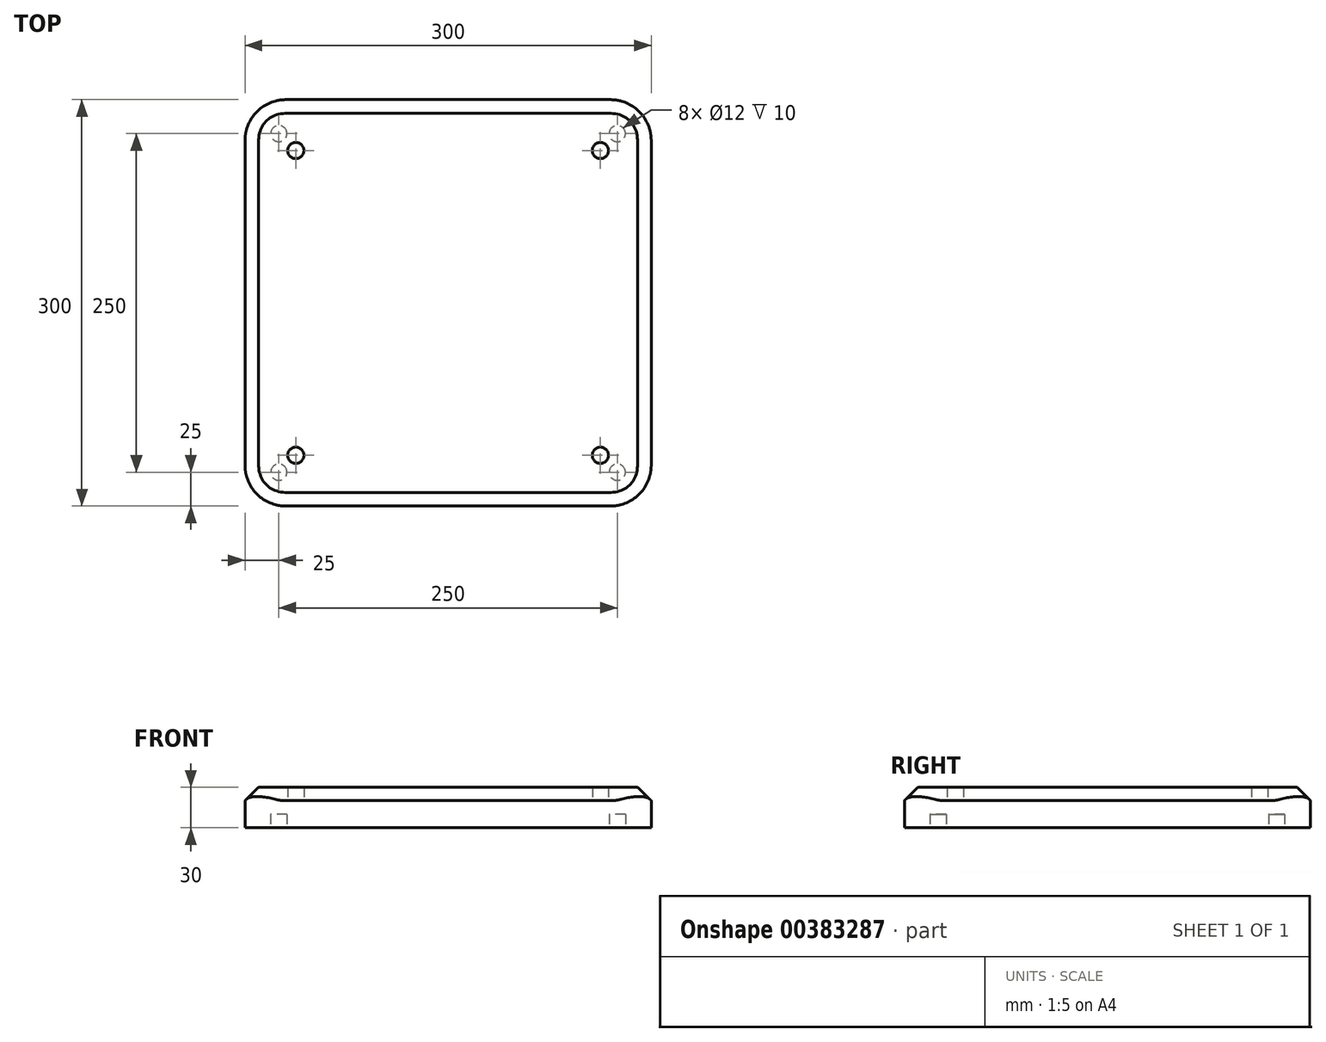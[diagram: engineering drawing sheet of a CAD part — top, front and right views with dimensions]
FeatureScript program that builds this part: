
annotation { "Feature Type Name" : "Feature", "Feature Type Description" : "" }
export const myFeature = defineFeature(function(context is Context, id is Id, definition is map)
    precondition{}
    {
        {
            var Q0;
            Q0=qCreatedBy(makeId("Top.planeOp"),FACE);
            var sketch = newSketch(context, id + "F0", { "sketchPlane" : qUnion([Q0])});
            skLineSegment(sketch, "E0.bottom", {"start": v(150, -150) * mm, "end": v(-150, -150) * mm});
            skLineSegment(sketch, "E0.top", {"start": v(150, 150) * mm, "end": v(-150, 150) * mm});
            skLineSegment(sketch, "E0.left", {"start": v(150, -150) * mm, "end": v(150, 150) * mm});
            skLineSegment(sketch, "E0.right", {"start": v(-150, -150) * mm, "end": v(-150, 150) * mm});
            skPoint(sketch, "E0.middle", {"position": v(0, 0) * mm});
            skCircle(sketch, "E1", {"center": v(-112.5, 112.5) * mm, "radius": 6 * mm});
            skCircle(sketch, "E2", {"center": v(-112.5, -112.5) * mm, "radius": 6 * mm});
            skCircle(sketch, "E3", {"center": v(112.5, 112.5) * mm, "radius": 6 * mm});
            skCircle(sketch, "E4", {"center": v(112.5, -112.5) * mm, "radius": 6 * mm});
            skLineSegment(sketch, "E5", {"start": v(-112.5, -150) * mm, "end": v(-112.5, 150) * mm, "construction": true});
            skLineSegment(sketch, "E6", {"start": v(112.5, -150) * mm, "end": v(112.5, 150) * mm, "construction": true});
            skLineSegment(sketch, "E7", {"start": v(-150, 112.5) * mm, "end": v(150, 112.5) * mm, "construction": true});
            skLineSegment(sketch, "E8", {"start": v(-150, -112.5) * mm, "end": v(150, -112.5) * mm, "construction": true});
            skCircle(sketch, "E9", {"center": v(-125, 125) * mm, "radius": 6 * mm});
            skCircle(sketch, "E10", {"center": v(-125, -125) * mm, "radius": 6 * mm});
            skCircle(sketch, "E11", {"center": v(125, -125) * mm, "radius": 6 * mm});
            skCircle(sketch, "E12", {"center": v(125, 125) * mm, "radius": 6 * mm});
            skLineSegment(sketch, "E13", {"start": v(-125, 150) * mm, "end": v(-125, -150) * mm, "construction": true});
            skLineSegment(sketch, "E14", {"start": v(-150, -125) * mm, "end": v(150, -125) * mm, "construction": true});
            skLineSegment(sketch, "E15", {"start": v(125, -150) * mm, "end": v(125, 150) * mm, "construction": true});
            skLineSegment(sketch, "E16", {"start": v(150, 125) * mm, "end": v(-150, 125) * mm, "construction": true});
            skSolve(sketch);
        }
        {
            var Q0;
            Q0 = qSketchRegion(id + "F0", true);
            var Q1;
            Q1=makeQuery(id+"F0.imprint","IMPRINT",FACE,{"disambiguationData":[TD([[makeQuery(id+"F0.imprint","IMPRINT",EDGE,{"derivedFrom":sQuery(id+"F0.wireOp",EDGE,"E10")}),1.0]])]});
            var Q2;
            Q2=makeQuery(id+"F0.imprint","IMPRINT",FACE,{"disambiguationData":[TD([[makeQuery(id+"F0.imprint","IMPRINT",EDGE,{"derivedFrom":sQuery(id+"F0.wireOp",EDGE,"E9")}),1.0]])]});
            var Q3;
            Q3=makeQuery(id+"F0.imprint","IMPRINT",FACE,{"disambiguationData":[TD([[makeQuery(id+"F0.imprint","IMPRINT",EDGE,{"derivedFrom":sQuery(id+"F0.wireOp",EDGE,"E12")}),1.0]])]});
            var Q4;
            Q4=makeQuery(id+"F0.imprint","IMPRINT",FACE,{"disambiguationData":[TD([[makeQuery(id+"F0.imprint","IMPRINT",EDGE,{"derivedFrom":sQuery(id+"F0.wireOp",EDGE,"E11")}),1.0]])]});
            extrude(context, id + "F1", {"entities" : qUnion([Q0, Q1, Q2, Q3, Q4]), "depth" : 30 * mm});
        }
        {
            var Q0;
            Q0=makeQuery(id+"F0.imprint","IMPRINT",FACE,{"disambiguationData":[TD([[makeQuery(id+"F0.imprint","IMPRINT",EDGE,{"derivedFrom":sQuery(id+"F0.wireOp",EDGE,"E10")}),1.0]])]});
            var Q1;
            Q1=makeQuery(id+"F0.imprint","IMPRINT",FACE,{"disambiguationData":[TD([[makeQuery(id+"F0.imprint","IMPRINT",EDGE,{"derivedFrom":sQuery(id+"F0.wireOp",EDGE,"E9")}),1.0]])]});
            var Q2;
            Q2=makeQuery(id+"F0.imprint","IMPRINT",FACE,{"disambiguationData":[TD([[makeQuery(id+"F0.imprint","IMPRINT",EDGE,{"derivedFrom":sQuery(id+"F0.wireOp",EDGE,"E12")}),1.0]])]});
            var Q3;
            Q3=makeQuery(id+"F0.imprint","IMPRINT",FACE,{"disambiguationData":[TD([[makeQuery(id+"F0.imprint","IMPRINT",EDGE,{"derivedFrom":sQuery(id+"F0.wireOp",EDGE,"E11")}),1.0]])]});
            extrude(context, id + "F2", {"entities" : qUnion([Q0, Q1, Q2, Q3]), "operationType" : NewBodyOperationType.REMOVE, "depth" : 10 * mm});
        }
        {
            var Q0;
            Q0=makeQuery(id+"F0.imprint","IMPRINT",FACE,{"disambiguationData":[TD([[makeQuery(id+"F0.imprint","IMPRINT",EDGE,{"derivedFrom":sQuery(id+"F0.wireOp",EDGE,"E1")}),1.0]])]});
            var Q1;
            Q1=makeQuery(id+"F0.imprint","IMPRINT",FACE,{"disambiguationData":[TD([[makeQuery(id+"F0.imprint","IMPRINT",EDGE,{"derivedFrom":sQuery(id+"F0.wireOp",EDGE,"E2")}),1.0]])]});
            var Q2;
            Q2=makeQuery(id+"F0.imprint","IMPRINT",FACE,{"disambiguationData":[TD([[makeQuery(id+"F0.imprint","IMPRINT",EDGE,{"derivedFrom":sQuery(id+"F0.wireOp",EDGE,"E3")}),1.0]])]});
            var Q3;
            Q3=makeQuery(id+"F0.imprint","IMPRINT",FACE,{"disambiguationData":[TD([[makeQuery(id+"F0.imprint","IMPRINT",EDGE,{"derivedFrom":sQuery(id+"F0.wireOp",EDGE,"E4")}),1.0]])]});
            extrude(context, id + "F3", {"entities" : qUnion([Q0, Q1, Q2, Q3]), "operationType" : NewBodyOperationType.ADD, "depth" : 20 * mm});
        }
        {
            var Q0;
            Q0=makeQuery(id+"F1.opExtrude","CAP_EDGE",EDGE,{"disambiguationData":[OSD([sQuery(id+"F0.wireOp",EDGE,"E0.bottom")])],"isStart":false});
            var Q1;
            Q1=makeQuery(id+"F1.opExtrude","CAP_EDGE",EDGE,{"disambiguationData":[OSD([sQuery(id+"F0.wireOp",EDGE,"E0.right")])],"isStart":false});
            var Q2;
            Q2=makeQuery(id+"F1.opExtrude","CAP_EDGE",EDGE,{"disambiguationData":[OSD([sQuery(id+"F0.wireOp",EDGE,"E0.left")])],"isStart":false});
            var Q3;
            Q3=makeQuery(id+"F1.opExtrude","CAP_EDGE",EDGE,{"disambiguationData":[OSD([sQuery(id+"F0.wireOp",EDGE,"E0.top")])],"isStart":false});
            chamfer(context, id + "F4", {"entities" : qUnion([Q0, Q1, Q2, Q3]), "chamferType" : ChamferType.OFFSET_ANGLE, "width" : 10 * mm, "oppositeDirection" : false, "angle" : 45 * degree, "tangentPropagation" : true});
        }
        {
            var Q0;
            Q0=makeQuery(id+"F4.opChamfer","BLEND_EDGE",EDGE,{"blendedFrom":[makeQuery(id+"F1.opExtrude","CAP_EDGE",EDGE,{"disambiguationData":[OSD([sQuery(id+"F0.wireOp",EDGE,"E0.bottom")])],"isStart":false}),makeQuery(id+"F1.opExtrude","CAP_EDGE",EDGE,{"disambiguationData":[OSD([sQuery(id+"F0.wireOp",EDGE,"E0.left")])],"isStart":false})],"blendedInto":[]});
            var Q1;
            Q1=makeQuery(id+"F4.opChamfer","BLEND_EDGE",EDGE,{"blendedFrom":[makeQuery(id+"F1.opExtrude","CAP_EDGE",EDGE,{"disambiguationData":[OSD([sQuery(id+"F0.wireOp",EDGE,"E0.bottom")])],"isStart":false}),makeQuery(id+"F1.opExtrude","CAP_EDGE",EDGE,{"disambiguationData":[OSD([sQuery(id+"F0.wireOp",EDGE,"E0.right")])],"isStart":false})],"blendedInto":[]});
            var Q2;
            Q2=makeQuery(id+"F4.opChamfer","BLEND_EDGE",EDGE,{"blendedFrom":[makeQuery(id+"F1.opExtrude","CAP_EDGE",EDGE,{"disambiguationData":[OSD([sQuery(id+"F0.wireOp",EDGE,"E0.top")])],"isStart":false}),makeQuery(id+"F1.opExtrude","CAP_EDGE",EDGE,{"disambiguationData":[OSD([sQuery(id+"F0.wireOp",EDGE,"E0.left")])],"isStart":false})],"blendedInto":[]});
            var Q3;
            Q3=makeQuery(id+"F4.opChamfer","BLEND_EDGE",EDGE,{"blendedFrom":[makeQuery(id+"F1.opExtrude","CAP_EDGE",EDGE,{"disambiguationData":[OSD([sQuery(id+"F0.wireOp",EDGE,"E0.top")])],"isStart":false}),makeQuery(id+"F1.opExtrude","CAP_EDGE",EDGE,{"disambiguationData":[OSD([sQuery(id+"F0.wireOp",EDGE,"E0.right")])],"isStart":false})],"blendedInto":[]});
            var Q4;
            Q4=makeQuery(id+"F1.opExtrude","SWEPT_EDGE",EDGE,{"disambiguationData":[OSD([sQuery(id+"F0.wireOp",EDGE,"E0.bottom"),sQuery(id+"F0.wireOp",EDGE,"E0.left")])]});
            var Q5;
            Q5=makeQuery(id+"F1.opExtrude","SWEPT_EDGE",EDGE,{"disambiguationData":[OSD([sQuery(id+"F0.wireOp",EDGE,"E0.bottom"),sQuery(id+"F0.wireOp",EDGE,"E0.right")])]});
            var Q6;
            Q6=makeQuery(id+"F1.opExtrude","SWEPT_EDGE",EDGE,{"disambiguationData":[OSD([sQuery(id+"F0.wireOp",EDGE,"E0.top"),sQuery(id+"F0.wireOp",EDGE,"E0.right")])]});
            var Q7;
            Q7=makeQuery(id+"F1.opExtrude","SWEPT_EDGE",EDGE,{"disambiguationData":[OSD([sQuery(id+"F0.wireOp",EDGE,"E0.top"),sQuery(id+"F0.wireOp",EDGE,"E0.left")])]});
            fillet(context, id + "F5", {"entities" : qUnion([Q0, Q1, Q2, Q3, Q4, Q5, Q6, Q7]), "radius" : 30 * mm, "tangentPropagation" : true, "allowEdgeOverflow" : false});
        }
    });
